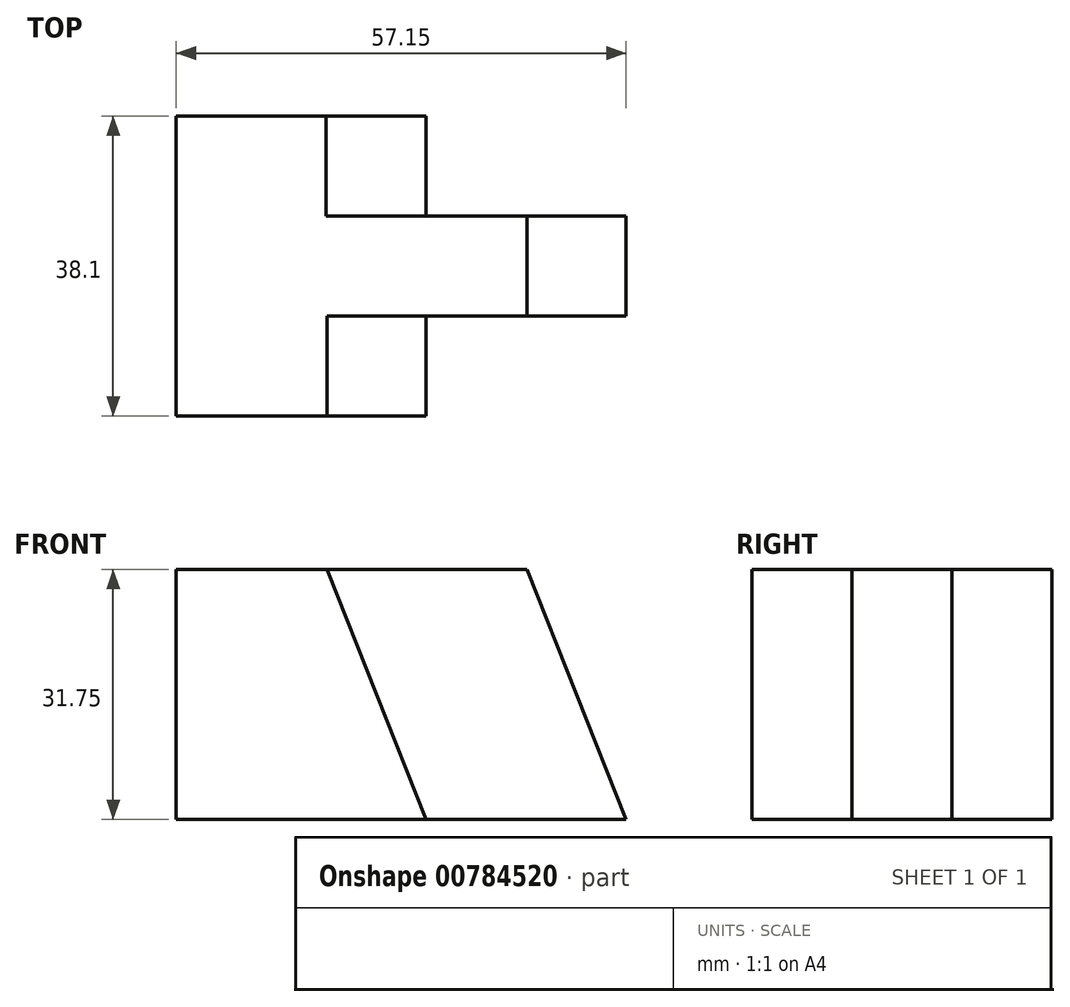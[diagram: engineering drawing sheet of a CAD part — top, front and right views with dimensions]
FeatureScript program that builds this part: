
annotation { "Feature Type Name" : "Feature", "Feature Type Description" : "" }
export const myFeature = defineFeature(function(context is Context, id is Id, definition is map)
    precondition{}
    {
        {
            var Q0;
            Q0=qCreatedBy(makeId("Front.planeOp"),FACE);
            var sketch = newSketch(context, id + "F0", { "sketchPlane" : qUnion([Q0])});
            skLineSegment(sketch, "E0", {"start": v(0, 0) * mm, "end": v(57.15, 0) * mm});
            skLineSegment(sketch, "E1", {"start": v(57.15, 0) * mm, "end": v(57.15, 31.75) * mm});
            skLineSegment(sketch, "E2", {"start": v(57.15, 31.75) * mm, "end": v(0, 31.75) * mm});
            skLineSegment(sketch, "E3", {"start": v(0, 31.75) * mm, "end": v(0, 0) * mm});
            skSolve(sketch);
        }
        {
            var Q0;
            Q0=makeQuery(id+"F0.imprint","IMPRINT",FACE,{"disambiguationData":[TD([[makeQuery(id+"F0.imprint","IMPRINT",EDGE,{"derivedFrom":sQuery(id+"F0.wireOp",EDGE,"E0")}),1.0]])]});
            extrude(context, id + "F1", {"entities" : qUnion([Q0]), "depth" : 38.1 * mm, "offsetDistance" : 25.4 * mm});
        }
        {
            var Q0;
            Q0=makeQuery(id+"F1.opExtrude","CAP_FACE",FACE,{"disambiguationData":[OSD([sQuery(id+"F0.wireOp",EDGE,"E0"),sQuery(id+"F0.wireOp",EDGE,"E1"),sQuery(id+"F0.wireOp",EDGE,"E2"),sQuery(id+"F0.wireOp",EDGE,"E3")])],"isStart":true});
            var sketch = newSketch(context, id + "F2", { "sketchPlane" : qUnion([Q0])});
            skLineSegment(sketch, "E4", {"start": v(0, 31.75) * mm, "end": v(-19.05, 31.75) * mm});
            skLineSegment(sketch, "E5", {"start": v(0, 0) * mm, "end": v(-31.75, 0) * mm});
            skLineSegment(sketch, "E6", {"start": v(-19.05, 31.75) * mm, "end": v(-31.75, 0) * mm});
            skSolve(sketch);
        }
        {
            var Q0;
            Q0=makeQuery(id+"F1.opExtrude","CAP_FACE",FACE,{"disambiguationData":[OSD([sQuery(id+"F0.wireOp",EDGE,"E0"),sQuery(id+"F0.wireOp",EDGE,"E1"),sQuery(id+"F0.wireOp",EDGE,"E2"),sQuery(id+"F0.wireOp",EDGE,"E3")])],"isStart":false});
            var sketch = newSketch(context, id + "F3", { "sketchPlane" : qUnion([Q0])});
            skLineSegment(sketch, "E7", {"start": v(19.14, 31.75) * mm, "end": v(31.74, 0) * mm});
            skLineSegment(sketch, "E8", {"start": v(31.74, 0) * mm, "end": v(57.14, 0) * mm});
            skLineSegment(sketch, "E9", {"start": v(19.14, 31.75) * mm, "end": v(44.54, 31.75) * mm});
            skLineSegment(sketch, "E10", {"start": v(44.54, 31.75) * mm, "end": v(57.15, 0) * mm});
            skSolve(sketch);
        }
        {
            var Q0;
            {var subQ0=sQuery(id+"F3.wireOp",EDGE,"E10");Q0=makeQuery(id+"F3.imprint","IMPRINT",FACE,{"disambiguationData":[TD([[makeQuery(id+"F3.imprint","IMPRINT",EDGE,{"derivedFrom":subQ0}),1.0]])]});}
            extrude(context, id + "F4", {"entities" : qUnion([Q0]), "operationType" : NewBodyOperationType.REMOVE, "oppositeDirection" : true, "depth" : 177.8 * mm, "offsetDistance" : 25.4 * mm});
        }
        {
            var Q0;
            Q0=makeQuery(id+"F3.imprint","IMPRINT",FACE,{"disambiguationData":[TD([[makeQuery(id+"F3.imprint","IMPRINT",EDGE,{"derivedFrom":sQuery(id+"F3.wireOp",EDGE,"E7")}),1.0]])]});
            extrude(context, id + "F5", {"entities" : qUnion([Q0]), "operationType" : NewBodyOperationType.REMOVE, "oppositeDirection" : true, "depth" : 12.7 * mm, "offsetDistance" : 25.4 * mm});
        }
        {
            var Q0;
            {var subQ0=sQuery(id+"F2.wireOp",EDGE,"E6");Q0=makeQuery(id+"F2.imprint","IMPRINT",FACE,{"disambiguationData":[TD([[makeQuery(id+"F2.imprint","IMPRINT",EDGE,{"derivedFrom":subQ0}),-1.0]])]});}
            extrude(context, id + "F6", {"entities" : qUnion([Q0]), "operationType" : NewBodyOperationType.REMOVE, "oppositeDirection" : true, "depth" : 12.7 * mm, "offsetDistance" : 25.4 * mm});
        }
    });
